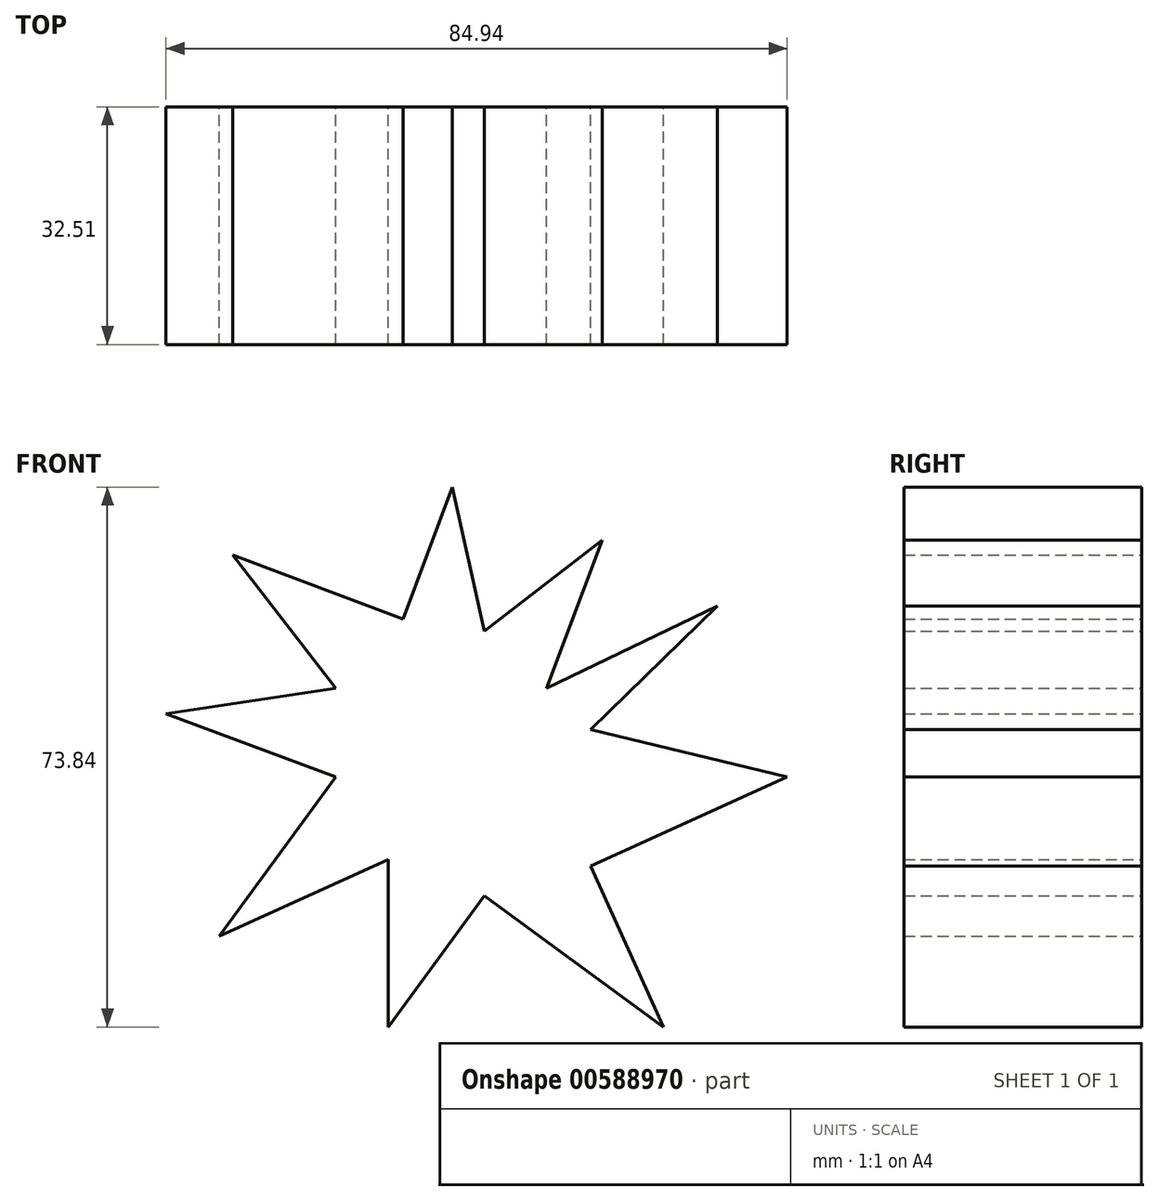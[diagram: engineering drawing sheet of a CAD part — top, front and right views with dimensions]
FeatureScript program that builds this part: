
annotation { "Feature Type Name" : "Feature", "Feature Type Description" : "" }
export const myFeature = defineFeature(function(context is Context, id is Id, definition is map)
    precondition{}
    {
        {
            var Q0;
            Q0=qCreatedBy(makeId("Front.planeOp"),FACE);
            var sketch = newSketch(context, id + "F0", { "sketchPlane" : qUnion([Q0])});
            skLineSegment(sketch, "E0", {"start": v(14.52, 22.75) * mm, "end": v(41.39, 16.25) * mm});
            skLineSegment(sketch, "E1", {"start": v(41.39, 16.25) * mm, "end": v(14.52, 4.09) * mm});
            skLineSegment(sketch, "E2", {"start": v(14.52, 4.09) * mm, "end": v(24.49, -17.94) * mm});
            skLineSegment(sketch, "E3", {"start": v(24.49, -17.94) * mm, "end": v(0, 0) * mm});
            skLineSegment(sketch, "E4", {"start": v(0, 0) * mm, "end": v(-13.14, -17.94) * mm});
            skLineSegment(sketch, "E5", {"start": v(-13.14, -17.94) * mm, "end": v(-13.14, 4.98) * mm});
            skLineSegment(sketch, "E6", {"start": v(-13.14, 4.98) * mm, "end": v(-36.28, -5.49) * mm});
            skLineSegment(sketch, "E7", {"start": v(-36.28, -5.49) * mm, "end": v(-20.35, 16.25) * mm});
            skLineSegment(sketch, "E8", {"start": v(-20.35, 16.25) * mm, "end": v(-43.55, 24.92) * mm});
            skLineSegment(sketch, "E9", {"start": v(-43.55, 24.92) * mm, "end": v(-20.35, 28.38) * mm});
            skLineSegment(sketch, "E10", {"start": v(-20.35, 28.38) * mm, "end": v(-34.45, 46.59) * mm});
            skLineSegment(sketch, "E11", {"start": v(-34.45, 46.59) * mm, "end": v(-11.12, 37.87) * mm});
            skLineSegment(sketch, "E12", {"start": v(-11.12, 37.87) * mm, "end": v(-4.39, 55.9) * mm});
            skLineSegment(sketch, "E13", {"start": v(-4.39, 55.9) * mm, "end": v(0, 36.18) * mm});
            skLineSegment(sketch, "E14", {"start": v(0, 36.18) * mm, "end": v(16.1, 48.65) * mm});
            skLineSegment(sketch, "E15", {"start": v(16.1, 48.65) * mm, "end": v(8.52, 28.38) * mm});
            skLineSegment(sketch, "E16", {"start": v(8.52, 28.38) * mm, "end": v(31.85, 39.65) * mm});
            skLineSegment(sketch, "E17", {"start": v(31.85, 39.65) * mm, "end": v(14.52, 22.75) * mm});
            skSolve(sketch);
        }
        {
            var Q0;
            Q0 = qSketchRegion(id + "F0", true);
            extrude(context, id + "F1", {"entities" : qUnion([Q0]), "depth" : 32.5 * mm, "offsetDistance" : 25.4 * mm});
        }
    });
